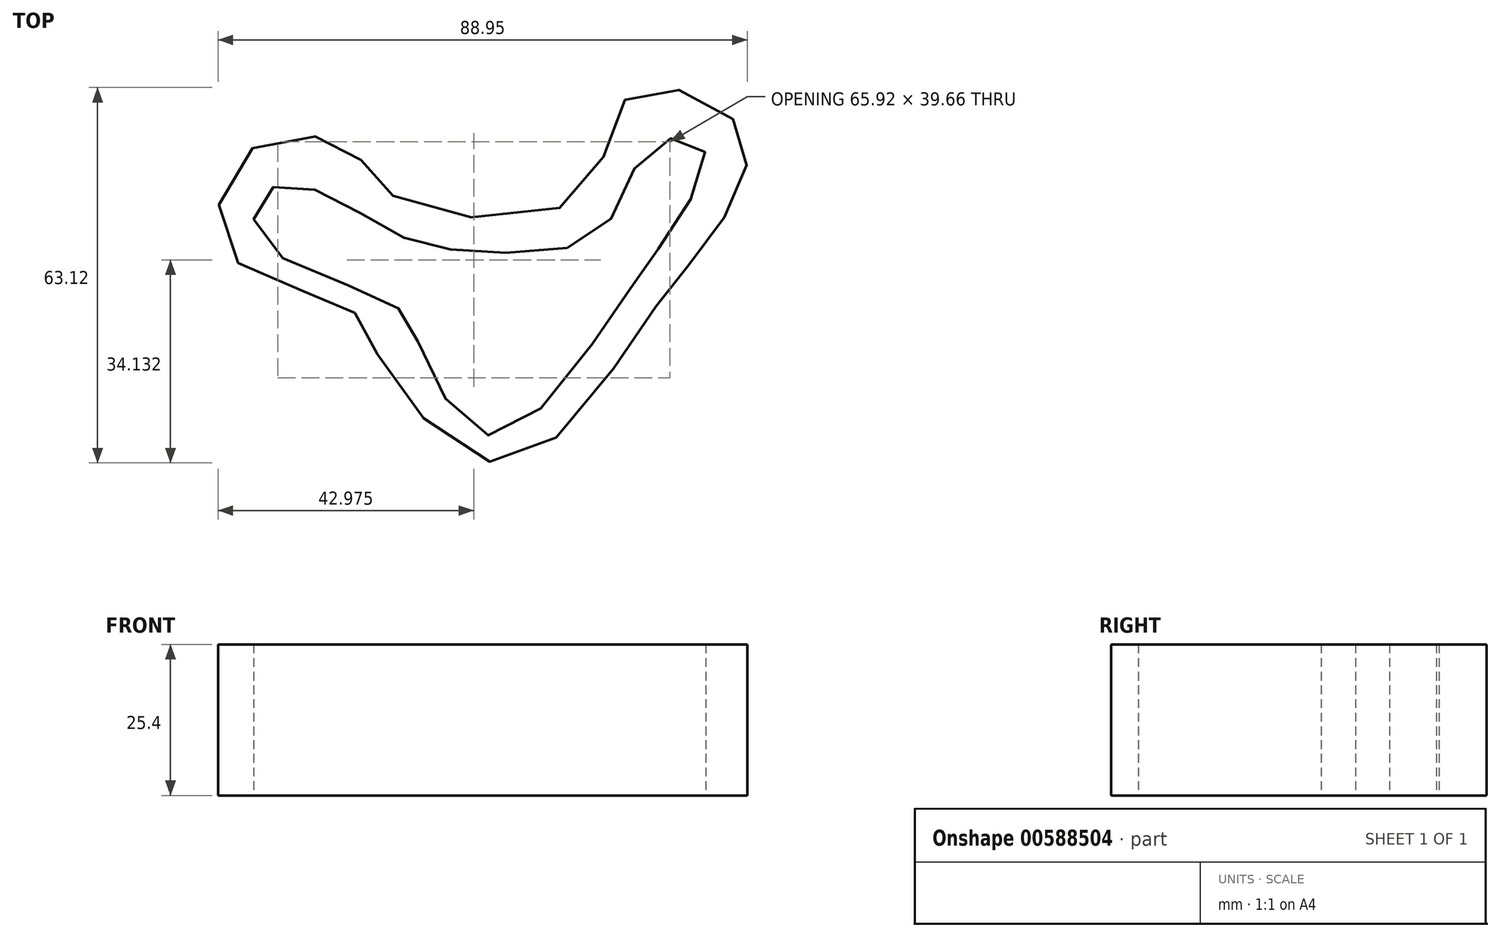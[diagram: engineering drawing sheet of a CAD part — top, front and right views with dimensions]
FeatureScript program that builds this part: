
annotation { "Feature Type Name" : "Feature", "Feature Type Description" : "" }
export const myFeature = defineFeature(function(context is Context, id is Id, definition is map)
    precondition{}
    {
        {
            var Q0;
            Q0=qCreatedBy(makeId("Top.planeOp"),FACE);
            var sketch = newSketch(context, id + "F0", { "sketchPlane" : qUnion([Q0])});
            skFitSpline(sketch, "E0", {"points": [v(-16.34, 32.83) * mm, v(-23.67, 40.77) * mm, v(-40.46, 40.46) * mm, v(-43.82, 23.06) * mm, v(-24.58, 14.5) * mm, v(-18.78, 5.95) * mm, v(2.3, -12.06) * mm, v(24.89, 9.92) * mm, v(34.36, 22.45) * mm, v(42.9, 36.8) * mm, v(39.24, 47.18) * mm, v(23.36, 49.62) * mm, v(15.12, 32.83) * mm, v(-16.34, 32.83) * mm]});
            skFitSpline(sketch, "E1", {"points": [v(-14.5, 25.8) * mm, v(0, 23.36) * mm, v(18.78, 27.03) * mm, v(27.03, 41.07) * mm, v(35.88, 40.77) * mm, v(29.77, 26.11) * mm, v(20.61, 12.98) * mm, v(0, -7.48) * mm, v(-12.06, 8.1) * mm, v(-17.25, 15.12) * mm, v(-38.63, 25.5) * mm, v(-37.4, 33.74) * mm, v(-27.64, 33.13) * mm, v(-14.5, 25.8) * mm]});
            skSolve(sketch);
        }
        {
            var Q0;
            Q0=makeQuery(id+"F0.imprint","IMPRINT",FACE,{"disambiguationData":[TD([[makeQuery(id+"F0.imprint","IMPRINT",EDGE,{"derivedFrom":sQuery(id+"F0.wireOp",EDGE,"E0")}),1.0]])]});
            extrude(context, id + "F1", {"entities" : qUnion([Q0]), "depth" : 25.4 * mm, "offsetDistance" : 25.4 * mm});
        }
    });
